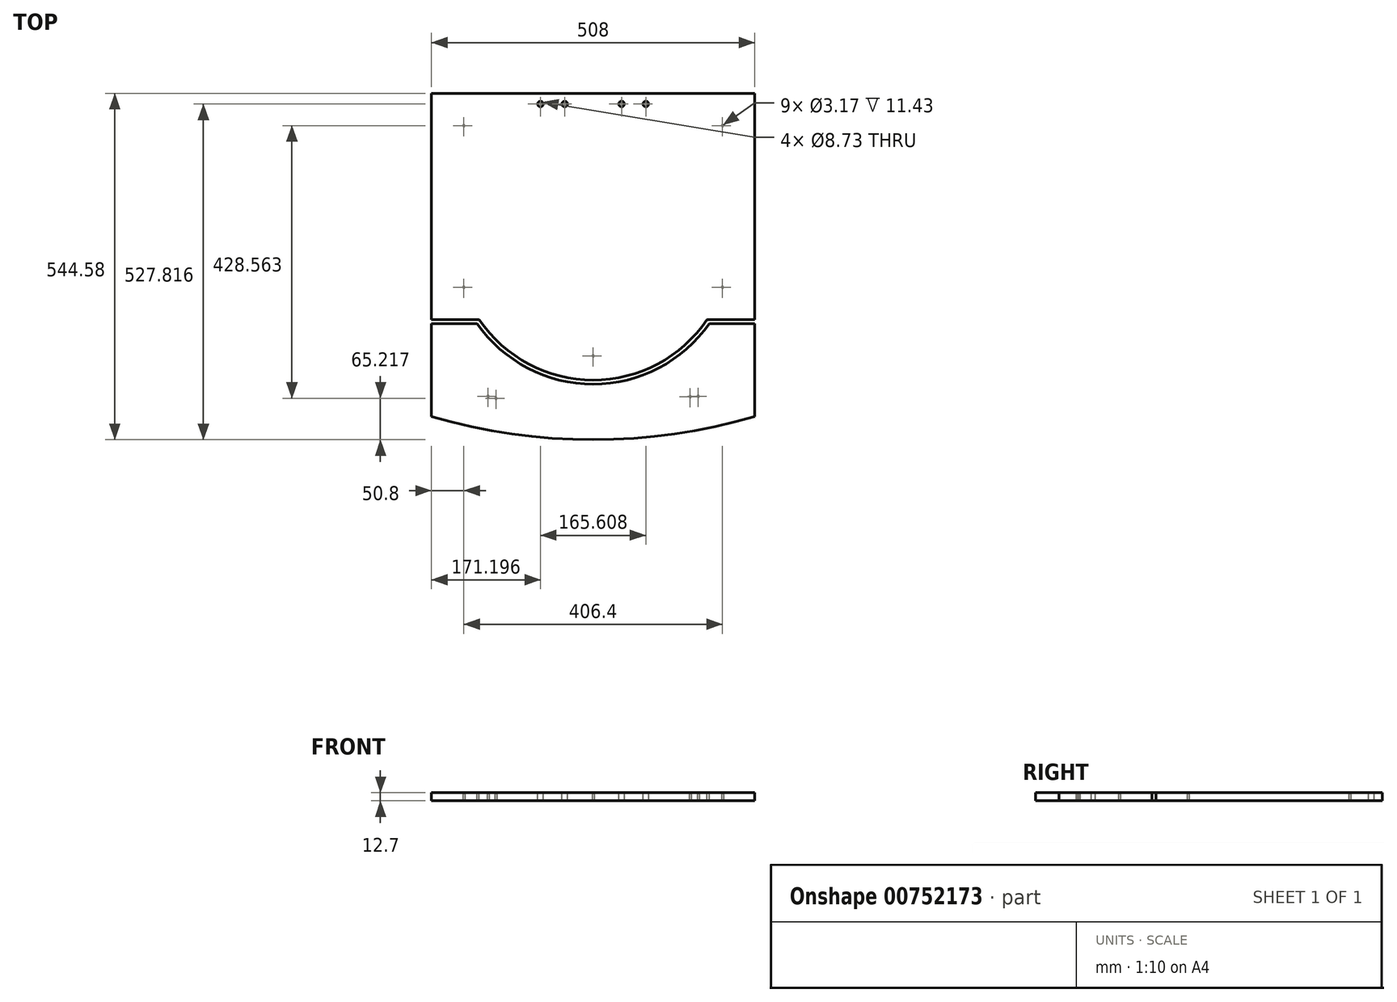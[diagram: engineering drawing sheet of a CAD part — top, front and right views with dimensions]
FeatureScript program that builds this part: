
annotation { "Feature Type Name" : "Feature", "Feature Type Description" : "" }
export const myFeature = defineFeature(function(context is Context, id is Id, definition is map)
    precondition{}
    {
        {
            var Q0;
            Q0=qCreatedBy(makeId("Top.planeOp"),FACE);
            var sketch = newSketch(context, id + "F0", { "sketchPlane" : qUnion([Q0])});
            skLineSegment(sketch, "E0.bottom", {"start": v(-304.8, 304.8) * mm, "end": v(304.8, 304.8) * mm, "construction": true});
            skLineSegment(sketch, "E0.top", {"start": v(-304.8, -304.8) * mm, "end": v(304.8, -304.8) * mm, "construction": true});
            skLineSegment(sketch, "E0.left", {"start": v(-304.8, 304.8) * mm, "end": v(-304.8, -304.8) * mm, "construction": true});
            skLineSegment(sketch, "E0.right", {"start": v(304.8, 304.8) * mm, "end": v(304.8, -304.8) * mm, "construction": true});
            skLineSegment(sketch, "E1.bottom", {"start": v(-254, 254) * mm, "end": v(254, 254) * mm});
            skLineSegment(sketch, "E1.top", {"start": v(-254, -254) * mm, "end": v(254, -254) * mm});
            skLineSegment(sketch, "E1.left", {"start": v(-254, 254) * mm, "end": v(-254, -254) * mm});
            skLineSegment(sketch, "E1.right", {"start": v(254, 254) * mm, "end": v(254, -254) * mm});
            skSolve(sketch);
        }
        {
            var Q0;
            Q0=makeQuery(id+"F0.imprint","IMPRINT",FACE,{"disambiguationData":[TD([[makeQuery(id+"F0.imprint","IMPRINT",EDGE,{"derivedFrom":sQuery(id+"F0.wireOp",EDGE,"E1.bottom")}),-1.0]])]});
            extrude(context, id + "F1", {"entities" : qUnion([Q0]), "depth" : 12.7 * mm, "offsetDistance" : 25.4 * mm});
        }
        {
            var Q0;
            Q0=makeQuery(id+"F1.opExtrude","CAP_FACE",FACE,{"disambiguationData":[OSD([sQuery(id+"F0.wireOp",EDGE,"E1.bottom"),sQuery(id+"F0.wireOp",EDGE,"E1.top"),sQuery(id+"F0.wireOp",EDGE,"E1.left"),sQuery(id+"F0.wireOp",EDGE,"E1.right")])],"isStart":false});
            var sketch = newSketch(context, id + "F2", { "sketchPlane" : qUnion([Q0])});
            skLineSegment(sketch, "E2", {"start": v(0, -22.25) * mm, "end": v(0, 32.58) * mm, "construction": true});
            skLineSegment(sketch, "E3", {"start": v(-16.2, 19.05) * mm, "end": v(0, 19.05) * mm, "construction": true});
            skCircle(sketch, "E4", {"center": v(0, 19.05) * mm, "radius": 200.03 * mm, "construction": true});
            skCircle(sketch, "E5", {"center": v(0, 19.05) * mm, "radius": 215.9 * mm});
            skArc(sketch, "E6", {"start": v(-182.39, -107.95) * mm, "mid": v(0, -203.2) * mm, "end": v(182.39, -107.95) * mm});
            skLineSegment(sketch, "E7.bottom", {"start": v(-254, -254) * mm, "end": v(254, -254) * mm});
            skLineSegment(sketch, "E7.top", {"start": v(-254, -101.6) * mm, "end": v(254, -101.6) * mm});
            skLineSegment(sketch, "E7.left", {"start": v(-254, -254) * mm, "end": v(-254, -101.6) * mm});
            skLineSegment(sketch, "E7.right", {"start": v(254, -254) * mm, "end": v(254, -101.6) * mm});
            skLineSegment(sketch, "E8", {"start": v(-254, -107.95) * mm, "end": v(-182.39, -107.95) * mm});
            skLineSegment(sketch, "E9.trimOffspring", {"start": v(-174.6, -107.95) * mm, "end": v(174.6, -107.95) * mm});
            skLineSegment(sketch, "E10.trimOffspring", {"start": v(182.39, -107.95) * mm, "end": v(254, -107.95) * mm});
            skArc(sketch, "E11.trimOffspring", {"start": v(186.65, -101.6) * mm, "mid": v(0, 241.3) * mm, "end": v(-186.65, -101.6) * mm});
            skSolve(sketch);
        }
        {
            var Q0;
            Q0=makeQuery(id+"F2.imprint","IMPRINT",FACE,{"disambiguationData":[TD([[makeQuery(id+"F2.imprint","IMPRINT",EDGE,{"derivedFrom":sQuery(id+"F2.wireOp",EDGE,"E6")}),1.0]])]});
            extrude(context, id + "F3", {"entities" : qUnion([Q0]), "operationType" : NewBodyOperationType.REMOVE, "oppositeDirection" : true, "depth" : 25.4 * mm, "offsetDistance" : 25.4 * mm});
        }
        {
            var Q0;
            {var subQ0=sQuery(id+"F0.wireOp",EDGE,"E1.left");var subQ1=sQuery(id+"F0.wireOp",EDGE,"E1.right");var subQ2=sQuery(id+"F0.wireOp",EDGE,"E1.top");Q0=makeQuery(id+"F3.boolean.opBoolean","SPLIT",FACE,{"disambiguationData":[TD([makeQuery(id+"F1.opExtrude","SWEPT_FACE",FACE,{"disambiguationData":[OSD([subQ2])]})])],"derivedFrom":makeQuery(id+"F1.opExtrude","CAP_FACE",FACE,{"disambiguationData":[OSD([sQuery(id+"F0.wireOp",EDGE,"E1.bottom"),subQ2,subQ0,subQ1])],"isStart":false})});}
            var sketch = newSketch(context, id + "F4", { "sketchPlane" : qUnion([Q0])});
            skLineSegment(sketch, "E12.bottom", {"start": v(-304.8, 304.8) * mm, "end": v(304.8, 304.8) * mm, "construction": true});
            skLineSegment(sketch, "E12.top", {"start": v(-304.8, -304.8) * mm, "end": v(304.8, -304.8) * mm, "construction": true});
            skLineSegment(sketch, "E12.left", {"start": v(-304.8, 304.8) * mm, "end": v(-304.8, -304.8) * mm, "construction": true});
            skLineSegment(sketch, "E12.right", {"start": v(304.8, 304.8) * mm, "end": v(304.8, -304.8) * mm, "construction": true});
            skLineSegment(sketch, "E13", {"start": v(-254, -254) * mm, "end": v(254, -254) * mm});
            skArc(sketch, "E14.trimOffspring", {"start": v(-254, -254) * mm, "mid": v(0, -290.58) * mm, "end": v(254, -254) * mm});
            skSolve(sketch);
        }
        {
            var Q0;
            Q0 = qSketchRegion(id + "F4", true);
            var Q1;
            {var subQ0=sQuery(id+"F0.wireOp",EDGE,"E1.left");var subQ1=sQuery(id+"F0.wireOp",EDGE,"E1.right");var subQ2=sQuery(id+"F0.wireOp",EDGE,"E1.top");Q1=makeQuery(id+"F3.boolean.opBoolean","SPLIT",FACE,{"disambiguationData":[TD([makeQuery(id+"F1.opExtrude","SWEPT_FACE",FACE,{"disambiguationData":[OSD([subQ2])]})])],"derivedFrom":makeQuery(id+"F1.opExtrude","CAP_FACE",FACE,{"disambiguationData":[OSD([sQuery(id+"F0.wireOp",EDGE,"E1.bottom"),subQ2,subQ0,subQ1])],"isStart":true})});}
            extrude(context, id + "F5", {"entities" : qUnion([Q0]), "operationType" : NewBodyOperationType.ADD, "endBound" : BoundingType.UP_TO_SURFACE, "oppositeDirection" : true, "depth" : 25.4 * mm, "endBoundEntityFace" : qUnion([Q1]), "offsetDistance" : 25.4 * mm});
        }
        {
            var Q0;
            {var subQ1=sQuery(id+"F0.wireOp",EDGE,"E1.left");var subQ2=sQuery(id+"F0.wireOp",EDGE,"E1.right");var subQ6=sQuery(id+"F0.wireOp",EDGE,"E1.bottom");Q0=makeQuery(id+"F3.boolean.opBoolean","SPLIT",FACE,{"disambiguationData":[TD([makeQuery(id+"F1.opExtrude","SWEPT_FACE",FACE,{"disambiguationData":[OSD([subQ6])]})])],"derivedFrom":makeQuery(id+"F1.opExtrude","CAP_FACE",FACE,{"disambiguationData":[OSD([subQ6,sQuery(id+"F0.wireOp",EDGE,"E1.top"),subQ1,subQ2])],"isStart":true})});}
            var sketch = newSketch(context, id + "F6", { "sketchPlane" : qUnion([Q0])});
            skLineSegment(sketch, "E15.bottom", {"start": v(203.2, -203.2) * mm, "end": v(-203.2, -203.2) * mm, "construction": true});
            skLineSegment(sketch, "E15.top", {"start": v(203.2, 50.8) * mm, "end": v(-203.2, 50.8) * mm, "construction": true});
            skLineSegment(sketch, "E15.left", {"start": v(203.2, -203.2) * mm, "end": v(203.2, 50.8) * mm, "construction": true});
            skLineSegment(sketch, "E15.right", {"start": v(-203.2, -203.2) * mm, "end": v(-203.2, 50.8) * mm, "construction": true});
            skCircle(sketch, "E16", {"center": v(0, -19.05) * mm, "radius": 177.8 * mm, "construction": true});
            skLineSegment(sketch, "E17", {"start": v(0, 25.6) * mm, "end": v(0, 185.62) * mm, "construction": true});
            skCircle(sketch, "E18", {"center": v(203.2, -203.2) * mm, "radius": 1.59 * mm});
            skCircle(sketch, "E19", {"center": v(-203.2, -203.2) * mm, "radius": 1.59 * mm});
            skCircle(sketch, "E20", {"center": v(-203.2, 50.8) * mm, "radius": 1.59 * mm});
            skCircle(sketch, "E21", {"center": v(203.2, 50.8) * mm, "radius": 1.59 * mm});
            skCircle(sketch, "E22", {"center": v(0, 158.75) * mm, "radius": 1.59 * mm});
            skCircle(sketch, "E23", {"center": v(152.4, 222.85) * mm, "radius": 1.59 * mm});
            skCircle(sketch, "E24", {"center": v(-152.62, 225.36) * mm, "radius": 1.59 * mm});
            skSolve(sketch);
        }
        {
            var Q0;
            Q0 = qSketchRegion(id + "F6", true);
            extrude(context, id + "F7", {"entities" : qUnion([Q0]), "operationType" : NewBodyOperationType.REMOVE, "oppositeDirection" : true, "depth" : 11.43 * mm, "offsetDistance" : 25.4 * mm});
        }
        {
            var Q0;
            {var subQ0=sQuery(id+"F0.wireOp",EDGE,"E1.right");var subQ1=sQuery(id+"F0.wireOp",EDGE,"E1.left");var subQ2=sQuery(id+"F0.wireOp",EDGE,"E1.top");var subQ3=sQuery(id+"F0.wireOp",EDGE,"E1.bottom");Q0=makeQuery(id+"F5.boolean.opBoolean","MERGE",FACE,{"derivedFrom":[makeQuery(id+"F3.boolean.opBoolean","SPLIT",FACE,{"disambiguationData":[TD([makeQuery(id+"F1.opExtrude","SWEPT_FACE",FACE,{"disambiguationData":[OSD([subQ2])]})])],"derivedFrom":makeQuery(id+"F1.opExtrude","CAP_FACE",FACE,{"disambiguationData":[OSD([subQ3,subQ2,subQ1,subQ0])],"isStart":true})}),makeQuery(id+"F5.opExtrude","CAP_FACE",FACE,{"disambiguationData":[OSD([subQ3,subQ2,subQ1,subQ0])],"isStart":false})]});}
            var sketch = newSketch(context, id + "F8", { "sketchPlane" : qUnion([Q0])});
            skLineSegment(sketch, "E25", {"start": v(-217.03, 222.25) * mm, "end": v(210.3, 222.25) * mm, "construction": true});
            skLineSegment(sketch, "E26", {"start": v(-165.1, 236.08) * mm, "end": v(-165.1, 195.76) * mm, "construction": true});
            skLineSegment(sketch, "E27", {"start": v(165.1, 241) * mm, "end": v(165.1, 199.2) * mm, "construction": true});
            skCircle(sketch, "E28", {"center": v(-165.1, 222.25) * mm, "radius": 1.59 * mm});
            skCircle(sketch, "E29", {"center": v(165.1, 222.25) * mm, "radius": 1.59 * mm});
            skSolve(sketch);
        }
        {
            var Q0;
            Q0 = qSketchRegion(id + "F8", true);
            extrude(context, id + "F9", {"entities" : qUnion([Q0]), "operationType" : NewBodyOperationType.REMOVE, "oppositeDirection" : true, "depth" : 11.43 * mm, "offsetDistance" : 25.4 * mm});
        }
        {
            var Q0;
            {var subQ1=sQuery(id+"F0.wireOp",EDGE,"E1.left");var subQ2=sQuery(id+"F0.wireOp",EDGE,"E1.right");var subQ6=sQuery(id+"F0.wireOp",EDGE,"E1.bottom");Q0=makeQuery(id+"F3.boolean.opBoolean","SPLIT",FACE,{"disambiguationData":[TD([makeQuery(id+"F1.opExtrude","SWEPT_FACE",FACE,{"disambiguationData":[OSD([subQ6])]})])],"derivedFrom":makeQuery(id+"F1.opExtrude","CAP_FACE",FACE,{"disambiguationData":[OSD([subQ6,sQuery(id+"F0.wireOp",EDGE,"E1.top"),subQ1,subQ2])],"isStart":false})});}
            var sketch = newSketch(context, id + "F10", { "sketchPlane" : qUnion([Q0])});
            skLineSegment(sketch, "E30", {"start": v(0, 271.7) * mm, "end": v(0, 114.13) * mm, "construction": true});
            skPoint(sketch, "E30.startSnap0", {"position": v(0, 254) * mm});
            skLineSegment(sketch, "E31", {"start": v(0, 249.94) * mm, "end": v(25.4, 249.94) * mm, "construction": true});
            skLineSegment(sketch, "E32", {"start": v(25.4, 249.94) * mm, "end": v(25.4, 224.54) * mm, "construction": true});
            skLineSegment(sketch, "E33", {"start": v(25.4, 224.54) * mm, "end": v(22.23, 224.54) * mm, "construction": true});
            skLineSegment(sketch, "E34", {"start": v(22.23, 224.54) * mm, "end": v(22.23, 246.76) * mm, "construction": true});
            skLineSegment(sketch, "E35", {"start": v(22.23, 246.76) * mm, "end": v(0, 246.76) * mm, "construction": true});
            skLineSegment(sketch, "E36", {"start": v(0, 246.76) * mm, "end": v(0, 249.94) * mm, "construction": true});
            skLineSegment(sketch, "E37.bottom", {"start": v(25.65, 253.91) * mm, "end": v(101.85, 253.91) * mm, "construction": true});
            skLineSegment(sketch, "E37.top", {"start": v(25.65, 220.56) * mm, "end": v(101.85, 220.56) * mm, "construction": true});
            skLineSegment(sketch, "E37.left", {"start": v(25.65, 253.91) * mm, "end": v(25.65, 220.56) * mm, "construction": true});
            skLineSegment(sketch, "E37.right", {"start": v(101.85, 253.91) * mm, "end": v(101.85, 220.56) * mm, "construction": true});
            skLineSegment(sketch, "E38", {"start": v(18.94, 237.24) * mm, "end": v(94.33, 237.24) * mm, "construction": true});
            skPoint(sketch, "E38.startSnap0", {"position": v(25.4, 237.24) * mm});
            skCircle(sketch, "E39", {"center": v(44.7, 237.24) * mm, "radius": 4.37 * mm});
            skCircle(sketch, "E40", {"center": v(82.8, 237.24) * mm, "radius": 4.37 * mm});
            skCircle(sketch, "E41.MirrorC", {"center": v(-44.7, 237.24) * mm, "radius": 4.37 * mm});
            skCircle(sketch, "E42.MirrorC", {"center": v(-82.8, 237.24) * mm, "radius": 4.37 * mm});
            skSolve(sketch);
        }
        {
            var Q0;
            Q0 = qSketchRegion(id + "F10", true);
            var Q1;
            {var subQ1=sQuery(id+"F0.wireOp",EDGE,"E1.left");var subQ2=sQuery(id+"F0.wireOp",EDGE,"E1.right");var subQ6=sQuery(id+"F0.wireOp",EDGE,"E1.bottom");Q1=makeQuery(id+"F3.boolean.opBoolean","SPLIT",FACE,{"disambiguationData":[TD([makeQuery(id+"F1.opExtrude","SWEPT_FACE",FACE,{"disambiguationData":[OSD([subQ6])]})])],"derivedFrom":makeQuery(id+"F1.opExtrude","CAP_FACE",FACE,{"disambiguationData":[OSD([subQ6,sQuery(id+"F0.wireOp",EDGE,"E1.top"),subQ1,subQ2])],"isStart":true})});}
            extrude(context, id + "F11", {"entities" : qUnion([Q0]), "operationType" : NewBodyOperationType.REMOVE, "endBound" : BoundingType.UP_TO_SURFACE, "oppositeDirection" : true, "depth" : 25.4 * mm, "endBoundEntityFace" : qUnion([Q1]), "offsetDistance" : 25.4 * mm});
        }
    });
